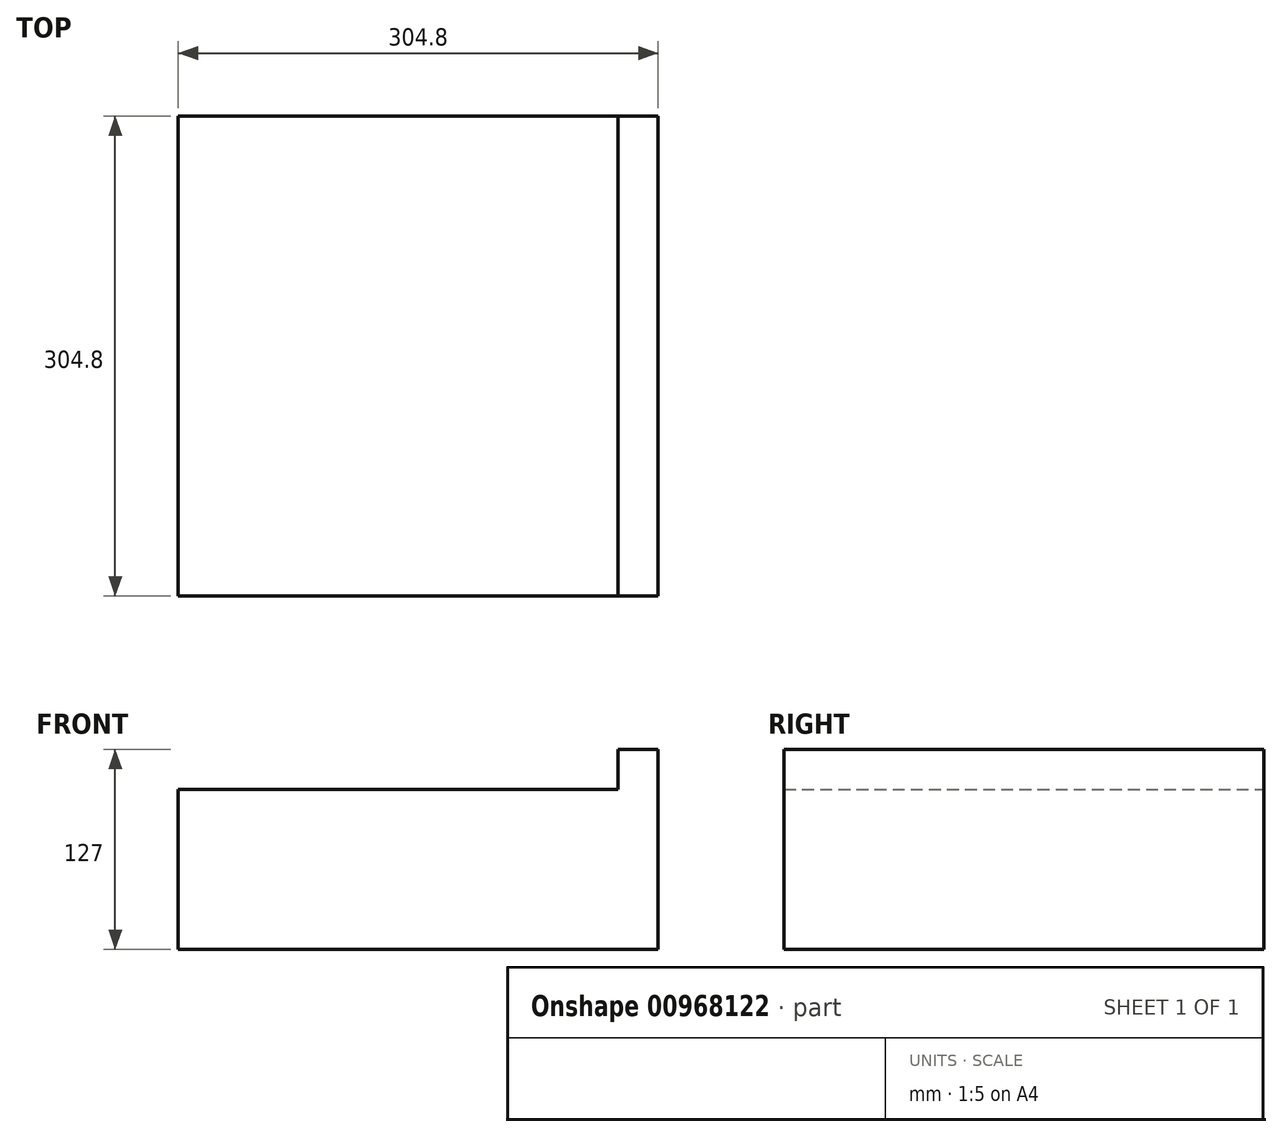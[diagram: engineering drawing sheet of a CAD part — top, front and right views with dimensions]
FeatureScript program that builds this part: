
annotation { "Feature Type Name" : "Feature", "Feature Type Description" : "" }
export const myFeature = defineFeature(function(context is Context, id is Id, definition is map)
    precondition{}
    {
        {
            var Q0;
            Q0=qCreatedBy(makeId("Front.planeOp"),FACE);
            var sketch = newSketch(context, id + "F0", { "sketchPlane" : qUnion([Q0])});
            skLineSegment(sketch, "E0.bottom", {"start": v(152.4, 50.8) * mm, "end": v(-152.4, 50.8) * mm});
            skLineSegment(sketch, "E0.top", {"start": v(152.4, -50.8) * mm, "end": v(-152.4, -50.8) * mm});
            skLineSegment(sketch, "E0.left", {"start": v(152.4, 50.8) * mm, "end": v(152.4, -50.8) * mm});
            skLineSegment(sketch, "E0.right", {"start": v(-152.4, 50.8) * mm, "end": v(-152.4, -50.8) * mm});
            skPoint(sketch, "E0.middle", {"position": v(0, 0) * mm});
            skLineSegment(sketch, "E1.bottom", {"start": v(152.4, 50.8) * mm, "end": v(127, 50.8) * mm});
            skLineSegment(sketch, "E1.top", {"start": v(152.4, 76.2) * mm, "end": v(127, 76.2) * mm});
            skLineSegment(sketch, "E1.left", {"start": v(152.4, 50.8) * mm, "end": v(152.4, 76.2) * mm});
            skLineSegment(sketch, "E1.right", {"start": v(127, 50.8) * mm, "end": v(127, 76.2) * mm});
            skSolve(sketch);
        }
        {
            var Q0;
            Q0 = qSketchRegion(id + "F0", true);
            extrude(context, id + "F1", {"entities" : qUnion([Q0]), "depth" : 304.8 * mm, "offsetDistance" : 25.4 * mm});
        }
    });
